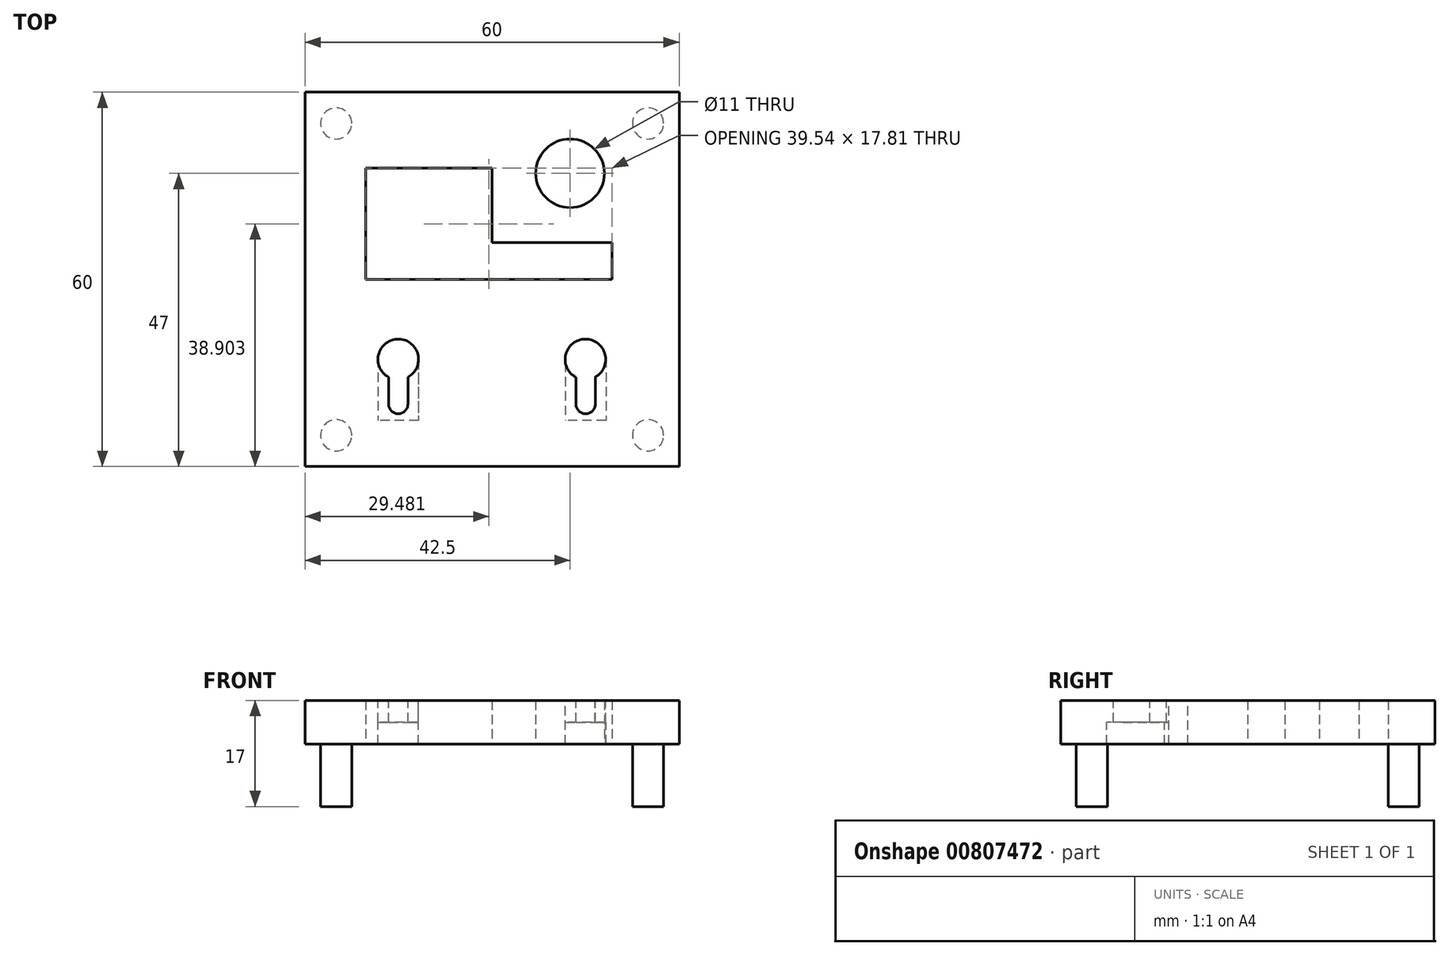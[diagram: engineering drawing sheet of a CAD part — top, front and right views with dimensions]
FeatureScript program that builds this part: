
annotation { "Feature Type Name" : "Feature", "Feature Type Description" : "" }
export const myFeature = defineFeature(function(context is Context, id is Id, definition is map)
    precondition{}
    {
        {
            var Q0;
            Q0=qCreatedBy(makeId("Top.planeOp"),FACE);
            var sketch = newSketch(context, id + "F0", { "sketchPlane" : qUnion([Q0])});
            skLineSegment(sketch, "E0.bottom", {"start": v(-25, 25) * mm, "end": v(25, 25) * mm, "construction": true});
            skLineSegment(sketch, "E0.top", {"start": v(-25, -25) * mm, "end": v(25, -25) * mm, "construction": true});
            skLineSegment(sketch, "E0.left", {"start": v(-25, 25) * mm, "end": v(-25, -25) * mm, "construction": true});
            skLineSegment(sketch, "E0.right", {"start": v(25, 25) * mm, "end": v(25, -25) * mm, "construction": true});
            skPoint(sketch, "E0.middle", {"position": v(0, 0) * mm});
            skLineSegment(sketch, "E1.bottom", {"start": v(-30, 30) * mm, "end": v(30, 30) * mm});
            skLineSegment(sketch, "E1.top", {"start": v(-30, -30) * mm, "end": v(30, -30) * mm});
            skLineSegment(sketch, "E1.left", {"start": v(-30, 30) * mm, "end": v(-30, -30) * mm});
            skLineSegment(sketch, "E1.right", {"start": v(30, 30) * mm, "end": v(30, -30) * mm});
            skCircle(sketch, "E2", {"center": v(-25, 25) * mm, "radius": 2.5 * mm});
            skCircle(sketch, "E3", {"center": v(25, 25) * mm, "radius": 2.5 * mm});
            skCircle(sketch, "E4", {"center": v(-25, -25) * mm, "radius": 2.5 * mm});
            skCircle(sketch, "E5", {"center": v(25, -25) * mm, "radius": 2.5 * mm});
            skLineSegment(sketch, "E6.bottom", {"start": v(25, 25) * mm, "end": v(12.5, 25) * mm, "construction": true});
            skLineSegment(sketch, "E6.top", {"start": v(25, 17) * mm, "end": v(12.5, 17) * mm, "construction": true});
            skLineSegment(sketch, "E6.left", {"start": v(25, 25) * mm, "end": v(25, 17) * mm, "construction": true});
            skLineSegment(sketch, "E6.right", {"start": v(12.5, 25) * mm, "end": v(12.5, 17) * mm, "construction": true});
            skCircle(sketch, "E7", {"center": v(12.5, 17) * mm, "radius": 5.5 * mm});
            skLineSegment(sketch, "E8.bottom", {"start": v(-20.3, 17.8) * mm, "end": v(0, 17.8) * mm});
            skLineSegment(sketch, "E8.top", {"start": v(-20.3, 0) * mm, "end": v(0, 0) * mm});
            skLineSegment(sketch, "E8.left", {"start": v(-20.3, 17.8) * mm, "end": v(-20.3, 0) * mm});
            skLineSegment(sketch, "E8.right", {"start": v(0, 17.8) * mm, "end": v(0, 0) * mm});
            skLineSegment(sketch, "E9.bottom", {"start": v(-20.3, 0) * mm, "end": v(19.25, 0) * mm});
            skLineSegment(sketch, "E9.top", {"start": v(-20.3, 5.93) * mm, "end": v(19.25, 5.93) * mm});
            skLineSegment(sketch, "E9.left", {"start": v(-20.3, 0) * mm, "end": v(-20.3, 5.93) * mm});
            skLineSegment(sketch, "E9.right", {"start": v(19.25, 0) * mm, "end": v(19.25, 5.93) * mm});
            skSolve(sketch);
        }
        {
            var Q0;
            Q0=makeQuery(id+"F0.imprint","IMPRINT",FACE,{"disambiguationData":[TD([[makeQuery(id+"F0.imprint","IMPRINT",EDGE,{"derivedFrom":sQuery(id+"F0.wireOp",EDGE,"E2")}),1.0]])]});
            var Q1;
            Q1=makeQuery(id+"F0.imprint","IMPRINT",FACE,{"disambiguationData":[TD([[makeQuery(id+"F0.imprint","IMPRINT",EDGE,{"derivedFrom":sQuery(id+"F0.wireOp",EDGE,"E3")}),1.0]])]});
            var Q2;
            Q2=makeQuery(id+"F0.imprint","IMPRINT",FACE,{"disambiguationData":[TD([[makeQuery(id+"F0.imprint","IMPRINT",EDGE,{"derivedFrom":sQuery(id+"F0.wireOp",EDGE,"E5")}),1.0]])]});
            var Q3;
            Q3=makeQuery(id+"F0.imprint","IMPRINT",FACE,{"disambiguationData":[TD([[makeQuery(id+"F0.imprint","IMPRINT",EDGE,{"derivedFrom":sQuery(id+"F0.wireOp",EDGE,"E4")}),1.0]])]});
            extrude(context, id + "F1", {"entities" : qUnion([Q0, Q1, Q2, Q3]), "oppositeDirection" : true, "depth" : 10 * mm, "offsetDistance" : 25 * mm});
        }
        {
            var Q0;
            Q0=makeQuery(id+"F0.imprint","IMPRINT",FACE,{"disambiguationData":[TD([[makeQuery(id+"F0.imprint","IMPRINT",EDGE,{"derivedFrom":sQuery(id+"F0.wireOp",EDGE,"E1.bottom")}),-1.0]])]});
            var Q1;
            Q1=makeQuery(id+"F0.imprint","IMPRINT",FACE,{"disambiguationData":[TD([[makeQuery(id+"F0.imprint","IMPRINT",EDGE,{"derivedFrom":sQuery(id+"F0.wireOp",EDGE,"E2")}),1.0]])]});
            var Q2;
            Q2=makeQuery(id+"F0.imprint","IMPRINT",FACE,{"disambiguationData":[TD([[makeQuery(id+"F0.imprint","IMPRINT",EDGE,{"derivedFrom":sQuery(id+"F0.wireOp",EDGE,"E4")}),1.0]])]});
            var Q3;
            Q3=makeQuery(id+"F0.imprint","IMPRINT",FACE,{"disambiguationData":[TD([[makeQuery(id+"F0.imprint","IMPRINT",EDGE,{"derivedFrom":sQuery(id+"F0.wireOp",EDGE,"E5")}),1.0]])]});
            var Q4;
            Q4=makeQuery(id+"F0.imprint","IMPRINT",FACE,{"disambiguationData":[TD([[makeQuery(id+"F0.imprint","IMPRINT",EDGE,{"derivedFrom":sQuery(id+"F0.wireOp",EDGE,"E3")}),1.0]])]});
            extrude(context, id + "F2", {"entities" : qUnion([Q0, Q1, Q2, Q3, Q4]), "depth" : 7 * mm, "offsetDistance" : 25 * mm});
        }
        {
            var Q0;
            Q0=makeQuery(id+"F2.opExtrude","CAP_FACE",FACE,{"disambiguationData":[OSD([sQuery(id+"F0.wireOp",EDGE,"E1.bottom"),sQuery(id+"F0.wireOp",EDGE,"E1.top"),sQuery(id+"F0.wireOp",EDGE,"E1.left"),sQuery(id+"F0.wireOp",EDGE,"E1.right"),sQuery(id+"F0.wireOp",EDGE,"E7")])],"isStart":false});
            var sketch = newSketch(context, id + "F3", { "sketchPlane" : qUnion([Q0])});
            skLineSegment(sketch, "E10.bottom", {"start": v(15, -20) * mm, "end": v(-15, -20) * mm, "construction": true});
            skLineSegment(sketch, "E10.top", {"start": v(15, 20) * mm, "end": v(-15, 20) * mm, "construction": true});
            skLineSegment(sketch, "E10.left", {"start": v(15, -20) * mm, "end": v(15, 20) * mm, "construction": true});
            skLineSegment(sketch, "E10.right", {"start": v(-15, -20) * mm, "end": v(-15, 20) * mm, "construction": true});
            skPoint(sketch, "E10.middle", {"position": v(0, 0) * mm});
            skCircle(sketch, "E11", {"center": v(15, -20) * mm, "radius": 1.55 * mm});
            skLineSegment(sketch, "E12.bottom", {"start": v(13.45, -20) * mm, "end": v(16.55, -20) * mm});
            skLineSegment(sketch, "E12.top", {"start": v(13.45, -15.67) * mm, "end": v(16.55, -15.67) * mm});
            skLineSegment(sketch, "E12.left", {"start": v(13.45, -20) * mm, "end": v(13.45, -15.67) * mm});
            skLineSegment(sketch, "E12.right", {"start": v(16.55, -20) * mm, "end": v(16.55, -15.67) * mm});
            skCircle(sketch, "E13", {"center": v(-15.05, -20) * mm, "radius": 1.55 * mm});
            skCircle(sketch, "E14", {"center": v(-15.05, -12.82) * mm, "radius": 3.25 * mm});
            skLineSegment(sketch, "E15.bottom", {"start": v(-16.6, -20) * mm, "end": v(-13.5, -20) * mm});
            skLineSegment(sketch, "E15.top", {"start": v(-16.6, -15.68) * mm, "end": v(-13.5, -15.68) * mm});
            skLineSegment(sketch, "E15.left", {"start": v(-16.6, -20) * mm, "end": v(-16.6, -15.68) * mm});
            skLineSegment(sketch, "E15.right", {"start": v(-13.5, -20) * mm, "end": v(-13.5, -15.68) * mm});
            skLineSegment(sketch, "E16.bottom", {"start": v(-11.8, -12.63) * mm, "end": v(-18.3, -12.63) * mm});
            skLineSegment(sketch, "E16.top", {"start": v(-11.8, -22.63) * mm, "end": v(-18.3, -22.63) * mm});
            skLineSegment(sketch, "E16.left", {"start": v(-11.8, -12.63) * mm, "end": v(-11.8, -22.63) * mm});
            skLineSegment(sketch, "E16.right", {"start": v(-18.3, -12.63) * mm, "end": v(-18.3, -22.63) * mm});
            skLineSegment(sketch, "E17.bottom", {"start": v(18.26, -12.63) * mm, "end": v(11.76, -12.63) * mm});
            skLineSegment(sketch, "E17.top", {"start": v(18.26, -22.63) * mm, "end": v(11.76, -22.63) * mm});
            skLineSegment(sketch, "E17.left", {"start": v(18.26, -12.63) * mm, "end": v(18.26, -22.63) * mm});
            skLineSegment(sketch, "E17.right", {"start": v(11.76, -12.63) * mm, "end": v(11.76, -22.63) * mm});
            skCircle(sketch, "E18", {"center": v(14.96, -12.82) * mm, "radius": 3.25 * mm});
            skSolve(sketch);
        }
        {
            var Q0;
            {var subQ0=sQuery(id+"F3.wireOp",EDGE,"E16.bottom");var subQ1=sQuery(id+"F3.wireOp",EDGE,"E14");var subQ3=makeQuery(id+"F3.imprint","INTERSECT",VERTEX,{"derivedFrom":[subQ1,subQ0]});Q0=makeQuery(id+"F3.imprint","IMPRINT",FACE,{"disambiguationData":[TD([[makeQuery(id+"F3.imprint","IMPRINT",EDGE,{"disambiguationData":[TD([[subQ3,1.0]])],"derivedFrom":subQ1}),1.0]])]});}
            var Q1;
            {var subQ5=sQuery(id+"F3.wireOp",EDGE,"E15.top");Q1=makeQuery(id+"F3.imprint","IMPRINT",FACE,{"disambiguationData":[TD([[makeQuery(id+"F3.imprint","IMPRINT",EDGE,{"derivedFrom":subQ5}),1.0]])]});}
            var Q2;
            {var subQ0=sQuery(id+"F3.wireOp",EDGE,"E15.top");Q2=makeQuery(id+"F3.imprint","IMPRINT",FACE,{"disambiguationData":[TD([[makeQuery(id+"F3.imprint","IMPRINT",EDGE,{"derivedFrom":subQ0}),-1.0]])]});}
            var Q3;
            {var subQ0=sQuery(id+"F3.wireOp",EDGE,"E15.left");Q3=makeQuery(id+"F3.imprint","IMPRINT",FACE,{"disambiguationData":[TD([[makeQuery(id+"F3.imprint","IMPRINT",EDGE,{"derivedFrom":subQ0}),-1.0]])]});}
            var Q4;
            {var subQ0=sQuery(id+"F3.wireOp",EDGE,"E15.bottom");Q4=makeQuery(id+"F3.imprint","IMPRINT",FACE,{"disambiguationData":[TD([[makeQuery(id+"F3.imprint","IMPRINT",EDGE,{"derivedFrom":subQ0}),1.0]])]});}
            var Q5;
            {var subQ0=sQuery(id+"F3.wireOp",EDGE,"E15.bottom");Q5=makeQuery(id+"F3.imprint","IMPRINT",FACE,{"disambiguationData":[TD([[makeQuery(id+"F3.imprint","IMPRINT",EDGE,{"derivedFrom":subQ0}),-1.0]])]});}
            var Q6;
            {var subQ0=sQuery(id+"F3.wireOp",EDGE,"E17.right");var subQ1=sQuery(id+"F3.wireOp",EDGE,"E17.bottom");var subQ2=makeQuery(id+"F3.imprint","INTERSECT",VERTEX,{"derivedFrom":[subQ1,subQ0]});Q6=makeQuery(id+"F3.imprint","IMPRINT",FACE,{"disambiguationData":[TD([[makeQuery(id+"F3.imprint","IMPRINT",EDGE,{"disambiguationData":[TD([[subQ2,1.0]])],"derivedFrom":subQ1}),-1.0]])]});}
            var Q7;
            {var subQ6=sQuery(id+"F3.wireOp",EDGE,"E12.left");var subQ7=sQuery(id+"F3.wireOp",EDGE,"E12.top");var subQ8=makeQuery(id+"F3.imprint","INTERSECT",VERTEX,{"derivedFrom":[subQ7,subQ6]});Q7=makeQuery(id+"F3.imprint","IMPRINT",FACE,{"disambiguationData":[TD([[makeQuery(id+"F3.imprint","IMPRINT",EDGE,{"disambiguationData":[TD([[subQ8,-1.0]])],"derivedFrom":subQ7}),1.0]])]});}
            var Q8;
            {var subQ0=sQuery(id+"F3.wireOp",EDGE,"E12.right");Q8=makeQuery(id+"F3.imprint","IMPRINT",FACE,{"disambiguationData":[TD([[makeQuery(id+"F3.imprint","IMPRINT",EDGE,{"derivedFrom":subQ0}),1.0]])]});}
            var Q9;
            {var subQ0=sQuery(id+"F3.wireOp",EDGE,"E12.left");var subQ1=sQuery(id+"F3.wireOp",EDGE,"E12.top");var subQ2=makeQuery(id+"F3.imprint","INTERSECT",VERTEX,{"derivedFrom":[subQ1,subQ0]});Q9=makeQuery(id+"F3.imprint","IMPRINT",FACE,{"disambiguationData":[TD([[makeQuery(id+"F3.imprint","IMPRINT",EDGE,{"disambiguationData":[TD([[subQ2,-1.0]])],"derivedFrom":subQ1}),-1.0]])]});}
            var Q10;
            {var subQ0=sQuery(id+"F3.wireOp",EDGE,"E12.bottom");Q10=makeQuery(id+"F3.imprint","IMPRINT",FACE,{"disambiguationData":[TD([[makeQuery(id+"F3.imprint","IMPRINT",EDGE,{"derivedFrom":subQ0}),1.0]])]});}
            var Q11;
            {var subQ0=sQuery(id+"F3.wireOp",EDGE,"E12.bottom");Q11=makeQuery(id+"F3.imprint","IMPRINT",FACE,{"disambiguationData":[TD([[makeQuery(id+"F3.imprint","IMPRINT",EDGE,{"derivedFrom":subQ0}),-1.0]])]});}
            extrude(context, id + "F4", {"entities" : qUnion([Q0, Q1, Q2, Q3, Q4, Q5, Q6, Q7, Q8, Q9, Q10, Q11]), "operationType" : NewBodyOperationType.REMOVE, "oppositeDirection" : true, "depth" : 25 * mm, "offsetDistance" : 25 * mm});
        }
        {
            var Q0;
            {var subQ0=sQuery(id+"F3.wireOp",EDGE,"E15.left");Q0=makeQuery(id+"F3.imprint","IMPRINT",FACE,{"disambiguationData":[TD([[makeQuery(id+"F3.imprint","IMPRINT",EDGE,{"derivedFrom":subQ0}),1.0]])]});}
            var Q1;
            {var subQ0=sQuery(id+"F3.wireOp",EDGE,"E12.right");Q1=makeQuery(id+"F3.imprint","IMPRINT",FACE,{"disambiguationData":[TD([[makeQuery(id+"F3.imprint","IMPRINT",EDGE,{"derivedFrom":subQ0}),-1.0]])]});}
            extrude(context, id + "F5", {"entities" : qUnion([Q0, Q1]), "operationType" : NewBodyOperationType.REMOVE, "oppositeDirection" : true, "depth" : 10 * mm, "offsetDistance" : 25 * mm});
        }
        {
            var Q0;
            {var subQ0=sQuery(id+"F3.wireOp",EDGE,"E15.left");Q0=makeQuery(id+"F3.imprint","IMPRINT",FACE,{"disambiguationData":[TD([[makeQuery(id+"F3.imprint","IMPRINT",EDGE,{"derivedFrom":subQ0}),1.0]])]});}
            var Q1;
            {var subQ0=sQuery(id+"F3.wireOp",EDGE,"E12.right");Q1=makeQuery(id+"F3.imprint","IMPRINT",FACE,{"disambiguationData":[TD([[makeQuery(id+"F3.imprint","IMPRINT",EDGE,{"derivedFrom":subQ0}),-1.0]])]});}
            extrude(context, id + "F6", {"entities" : qUnion([Q0, Q1]), "operationType" : NewBodyOperationType.ADD, "oppositeDirection" : true, "depth" : 3.5 * mm, "offsetDistance" : 25 * mm});
        }
    });
